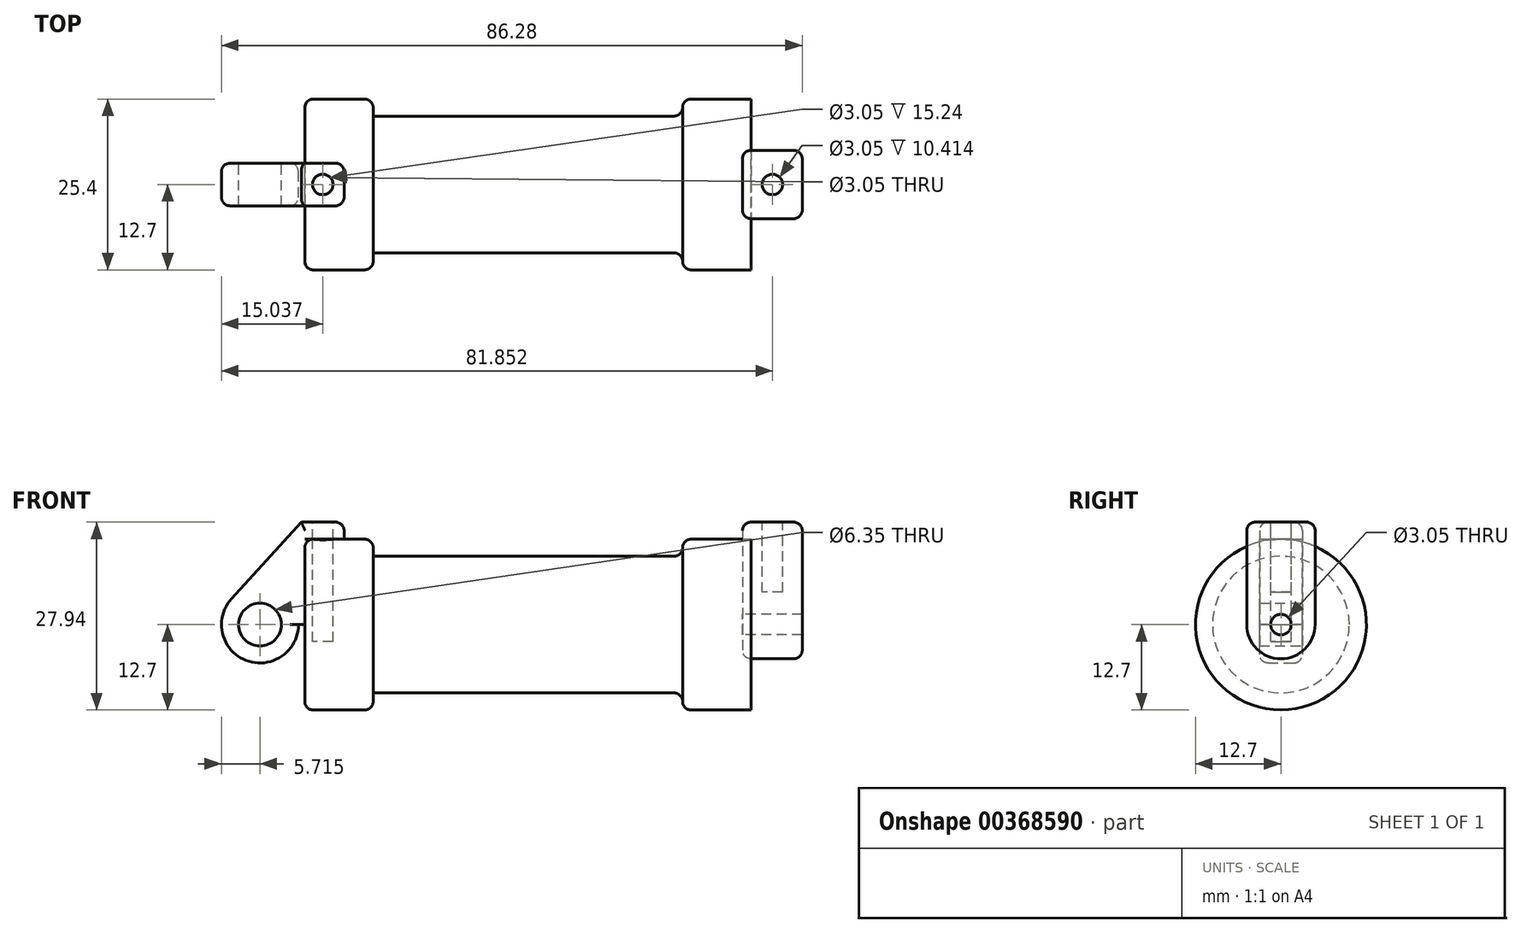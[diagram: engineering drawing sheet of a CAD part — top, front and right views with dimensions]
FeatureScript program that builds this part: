
annotation { "Feature Type Name" : "Feature", "Feature Type Description" : "" }
export const myFeature = defineFeature(function(context is Context, id is Id, definition is map)
    precondition{}
    {
        {
            var Q0;
            Q0=qCreatedBy(makeId("Front.planeOp"),FACE);
            var sketch = newSketch(context, id + "F0", { "sketchPlane" : qUnion([Q0])});
            skLineSegment(sketch, "E0", {"start": v(0, 0) * mm, "end": v(0, 12.7) * mm});
            skLineSegment(sketch, "E1", {"start": v(0, 12.7) * mm, "end": v(10.16, 12.7) * mm});
            skLineSegment(sketch, "E2", {"start": v(10.16, 12.7) * mm, "end": v(10.16, 10.16) * mm});
            skLineSegment(sketch, "E3", {"start": v(10.16, 10.16) * mm, "end": v(56.13, 10.16) * mm});
            skLineSegment(sketch, "E4", {"start": v(56.13, 10.16) * mm, "end": v(56.13, 12.7) * mm});
            skLineSegment(sketch, "E5", {"start": v(56.13, 12.7) * mm, "end": v(66.3, 12.7) * mm});
            skLineSegment(sketch, "E6", {"start": v(66.3, 12.7) * mm, "end": v(66.3, 0) * mm});
            skLineSegment(sketch, "E7", {"start": v(66.3, 0) * mm, "end": v(0, 0) * mm});
            skLineSegment(sketch, "E8", {"start": v(5.84, 15.24) * mm, "end": v(-0.5, 15.24) * mm});
            skLineSegment(sketch, "E9", {"start": v(-0.5, 15.24) * mm, "end": v(-10.88, 3.85) * mm});
            skLineSegment(sketch, "E10", {"start": v(0, 0) * mm, "end": v(-6.65, 0) * mm});
            skCircle(sketch, "E11", {"center": v(-6.65, 0) * mm, "radius": 5.72 * mm});
            skCircle(sketch, "E12", {"center": v(-6.65, 0) * mm, "radius": 3.18 * mm});
            skLineSegment(sketch, "E13", {"start": v(5.84, 15.24) * mm, "end": v(5.84, -9.4) * mm});
            skLineSegment(sketch, "E14", {"start": v(5.84, -9.4) * mm, "end": v(-8.18, -5.5) * mm});
            skSolve(sketch);
        }
        {
            var Q0;
            {var subQ5=sQuery(id+"F0.wireOp",EDGE,"E12");Q0=makeQuery(id+"F0.imprint","IMPRINT",FACE,{"disambiguationData":[TD([[makeQuery(id+"F0.imprint","IMPRINT",EDGE,{"derivedFrom":subQ5}),-1.0]])]});}
            var Q1;
            {var subQ1=sQuery(id+"F0.wireOp",EDGE,"E0");Q1=makeQuery(id+"F0.imprint","IMPRINT",FACE,{"disambiguationData":[TD([[makeQuery(id+"F0.imprint","IMPRINT",EDGE,{"derivedFrom":subQ1}),1.0]])]});}
            extrude(context, id + "F1", {"entities" : qUnion([Q0, Q1]), "endBound" : BoundingType.SYMMETRIC, "depth" : 6.35 * mm});
        }
        {
            var Q0;
            {var subQ0=sQuery(id+"F0.wireOp",EDGE,"E2");Q0=makeQuery(id+"F0.imprint","IMPRINT",FACE,{"disambiguationData":[TD([[makeQuery(id+"F0.imprint","IMPRINT",EDGE,{"derivedFrom":subQ0}),-1.0]])]});}
            var Q1;
            {var subQ0=sQuery(id+"F0.wireOp",EDGE,"E0");Q1=makeQuery(id+"F0.imprint","IMPRINT",FACE,{"disambiguationData":[TD([[makeQuery(id+"F0.imprint","IMPRINT",EDGE,{"derivedFrom":subQ0}),-1.0]])]});}
            var Q2;
            Q2=sQuery(id+"F0.wireOp",EDGE,"E7");
            revolve(context, id + "F2", {"entities" : qUnion([Q0, Q1]), "axis" : qUnion([Q2]), "revolveType" : RevolveType.FULL});
        }
        {
            var Q0;
            Q0=makeQuery(id+"F2.opRevolve","SWEPT_FACE",FACE,{"disambiguationData":[OSD([sQuery(id+"F0.wireOp",EDGE,"E6")])]});
            var sketch = newSketch(context, id + "F3", { "sketchPlane" : qUnion([Q0])});
            skCircle(sketch, "E15", {"center": v(0, 0) * mm, "radius": 5.08 * mm});
            skCircle(sketch, "E16", {"center": v(0, 0) * mm, "radius": 1.52 * mm});
            skLineSegment(sketch, "E17", {"start": v(-5.08, 15.24) * mm, "end": v(5.08, 15.24) * mm});
            skLineSegment(sketch, "E18", {"start": v(5.08, 15.24) * mm, "end": v(5.08, 0) * mm});
            skLineSegment(sketch, "E19", {"start": v(-5.08, 15.24) * mm, "end": v(-5.08, 0) * mm});
            skSolve(sketch);
        }
        {
            var Q0;
            {var subQ0=sQuery(id+"F3.wireOp",EDGE,"E17");Q0=makeQuery(id+"F3.imprint","IMPRINT",FACE,{"disambiguationData":[TD([[makeQuery(id+"F3.imprint","IMPRINT",EDGE,{"derivedFrom":subQ0}),-1.0]])]});}
            var Q1;
            {var subQ0=sQuery(id+"F3.wireOp",EDGE,"E18");var subQ1=sQuery(id+"F3.wireOp",EDGE,"E15");var subQ2=makeQuery(id+"F3.imprint","INTERSECT",VERTEX,{"derivedFrom":[subQ1,subQ0]});Q1=makeQuery(id+"F3.imprint","IMPRINT",FACE,{"disambiguationData":[TD([[makeQuery(id+"F3.imprint","IMPRINT",EDGE,{"disambiguationData":[TD([[subQ2,-1.0]])],"derivedFrom":subQ1}),-1.0]])]});}
            var Q2;
            Q2=makeQuery(id+"F3.imprint","IMPRINT",FACE,{"disambiguationData":[TD([[makeQuery(id+"F3.imprint","IMPRINT",EDGE,{"derivedFrom":sQuery(id+"F3.wireOp",EDGE,"E16")}),-1.0]])]});
            extrude(context, id + "F4", {"entities" : qUnion([Q0, Q1, Q2]), "depth" : 7.62 * mm, "hasSecondDirection" : true, "secondDirectionOppositeDirection" : true, "secondDirectionDepth" : 1.27 * mm});
        }
        {
            var Q0;
            Q0=makeQuery(id+"F1.opExtrude","SWEPT_FACE",FACE,{"disambiguationData":[OSD([sQuery(id+"F0.wireOp",EDGE,"E8")])]});
            var sketch = newSketch(context, id + "F5", { "sketchPlane" : qUnion([Q0])});
            skCircle(sketch, "E20", {"center": v(2.67, 0) * mm, "radius": 1.52 * mm});
            skPoint(sketch, "E20.centerSnap0", {"position": v(5.84, 0) * mm});
            skCircle(sketch, "E21", {"center": v(69.48, 0) * mm, "radius": 1.52 * mm});
            skSolve(sketch);
        }
        {
            var Q0;
            Q0=makeQuery(id+"F5.imprint","IMPRINT",FACE,{"disambiguationData":[TD([[makeQuery(id+"F5.imprint","IMPRINT",EDGE,{"derivedFrom":sQuery(id+"F5.wireOp",EDGE,"E20")}),1.0]])]});
            extrude(context, id + "F6", {"entities" : qUnion([Q0]), "operationType" : NewBodyOperationType.REMOVE, "oppositeDirection" : true, "depth" : 17.78 * mm});
        }
        {
            var Q0;
            Q0=makeQuery(id+"F5.imprint","IMPRINT",FACE,{"disambiguationData":[TD([[makeQuery(id+"F5.imprint","IMPRINT",EDGE,{"derivedFrom":sQuery(id+"F5.wireOp",EDGE,"E21")}),1.0]])]});
            extrude(context, id + "F7", {"entities" : qUnion([Q0]), "operationType" : NewBodyOperationType.REMOVE, "oppositeDirection" : true, "depth" : 10.4 * mm});
        }
        {
            var Q0;
            Q0=makeQuery(id+"F2.opRevolve","SWEPT_EDGE",EDGE,{"disambiguationData":[OSD([sQuery(id+"F0.wireOp",EDGE,"E1"),sQuery(id+"F0.wireOp",EDGE,"E2")])]});
            var Q1;
            Q1=makeQuery(id+"F1.opExtrude","CAP_EDGE",EDGE,{"disambiguationData":[OSD([sQuery(id+"F0.wireOp",EDGE,"E8")])],"isStart":false});
            var Q2;
            Q2=makeQuery(id+"F1.opExtrude","SWEPT_EDGE",EDGE,{"disambiguationData":[OSD([sQuery(id+"F0.wireOp",EDGE,"E8"),sQuery(id+"F0.wireOp",EDGE,"E13")])]});
            var Q3;
            Q3=makeQuery(id+"F1.opExtrude","CAP_EDGE",EDGE,{"disambiguationData":[OSD([sQuery(id+"F0.wireOp",EDGE,"E8")])],"isStart":true});
            var Q4;
            Q4=makeQuery(id+"F1.opExtrude","CAP_EDGE",EDGE,{"disambiguationData":[OSD([sQuery(id+"F0.wireOp",EDGE,"E9")])],"isStart":false});
            var Q5;
            Q5=makeQuery(id+"F1.opExtrude","CAP_EDGE",EDGE,{"disambiguationData":[OSD([sQuery(id+"F0.wireOp",EDGE,"E9")])],"isStart":true});
            var Q6;
            Q6=makeQuery(id+"F2.opRevolve","SWEPT_EDGE",EDGE,{"disambiguationData":[OSD([sQuery(id+"F0.wireOp",EDGE,"E4"),sQuery(id+"F0.wireOp",EDGE,"E5")])]});
            var Q7;
            Q7=makeQuery(id+"F2.opRevolve","SWEPT_EDGE",EDGE,{"disambiguationData":[OSD([sQuery(id+"F0.wireOp",EDGE,"E3"),sQuery(id+"F0.wireOp",EDGE,"E4")])]});
            var Q8;
            Q8=makeQuery(id+"F4.opExtrude","SWEPT_EDGE",EDGE,{"disambiguationData":[OSD([sQuery(id+"F3.wireOp",EDGE,"E17"),sQuery(id+"F3.wireOp",EDGE,"E18")])]});
            var Q9;
            Q9=makeQuery(id+"F4.opExtrude","CAP_EDGE",EDGE,{"disambiguationData":[OSD([sQuery(id+"F3.wireOp",EDGE,"E18")])],"isStart":false});
            var Q10;
            Q10=makeQuery(id+"F4.opExtrude","CAP_EDGE",EDGE,{"disambiguationData":[OSD([sQuery(id+"F3.wireOp",EDGE,"E15")])],"isStart":false});
            var Q11;
            Q11=makeQuery(id+"F4.opExtrude","CAP_EDGE",EDGE,{"disambiguationData":[OSD([sQuery(id+"F3.wireOp",EDGE,"E17")])],"isStart":false});
            var Q12;
            Q12=makeQuery(id+"F4.opExtrude","CAP_EDGE",EDGE,{"disambiguationData":[OSD([sQuery(id+"F3.wireOp",EDGE,"E17")])],"isStart":true});
            var Q13;
            Q13=makeQuery(id+"F4.opExtrude","CAP_EDGE",EDGE,{"disambiguationData":[OSD([sQuery(id+"F3.wireOp",EDGE,"E19")])],"isStart":true});
            var Q14;
            Q14=makeQuery(id+"F4.opExtrude","SWEPT_EDGE",EDGE,{"disambiguationData":[OSD([sQuery(id+"F3.wireOp",EDGE,"E17"),sQuery(id+"F3.wireOp",EDGE,"E19")])]});
            var Q15;
            Q15=makeQuery(id+"F2.opRevolve","SWEPT_EDGE",EDGE,{"disambiguationData":[OSD([sQuery(id+"F0.wireOp",EDGE,"E0"),sQuery(id+"F0.wireOp",EDGE,"E1")])]});
            var Q16;
            Q16=makeQuery(id+"F1.opExtrude","CAP_EDGE",EDGE,{"disambiguationData":[OSD([sQuery(id+"F0.wireOp",EDGE,"E13")])],"isStart":true});
            var Q17;
            Q17=makeQuery(id+"F1.opExtrude","CAP_EDGE",EDGE,{"disambiguationData":[OSD([sQuery(id+"F0.wireOp",EDGE,"E13")])],"isStart":false});
            var Q18;
            Q18=makeQuery(id+"F4.opExtrude","CAP_EDGE",EDGE,{"disambiguationData":[OSD([sQuery(id+"F3.wireOp",EDGE,"E19")])],"isStart":false});
            fillet(context, id + "F8", {"entities" : qUnion([Q0, Q1, Q2, Q3, Q4, Q5, Q6, Q7, Q8, Q9, Q10, Q11, Q12, Q13, Q14, Q15, Q16, Q17, Q18]), "radius" : 1.27 * mm, "tangentPropagation" : true, "allowEdgeOverflow" : false});
        }
    });
